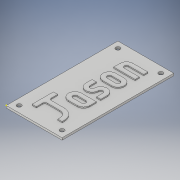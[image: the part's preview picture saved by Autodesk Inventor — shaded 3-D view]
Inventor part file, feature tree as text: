
AUTODESK INVENTOR PART (.ipt)
format: ipt  version: 2017 (Build 210142000, 142)  size: 196,096 bytes
history: native  units: in
note: dims shown in document units (in); Inventor stores cm internally (conversion verified against a paired STEP export)
features: sketch x4, extrude x3, projected_geometry x1
ambient origin geometry x8: Origin, YZ Plane, XZ Plane, XY Plane, X Axis, Y Axis, Z Axis, Center Point
bodies: Solid1 (feature_tree)
feature tree (8):
  extrude  "Extrusion1"  Depth=0.0625in TaperAngle=0.0deg
  sketch  "Sketch2"  dims[d6=0.0625in d7=0.0in]
  sketch  "Sketch3"
  extrude  "Extrusion2"  [1 undecoded]
  extrude  "Extrusion3"  [1 undecoded]
  sketch  "Sketch1"  dims[d2=0.125in d3=0.0in d4=0.0625in d5=0.0in]
  sketch  "Sketch4"
  projected_geometry  "Projected Loop1"
note: 2 required parameter values undecoded (feature->parameter linkage not recoverable at this tier; creation-order binding heuristic only, values carry confidence <= 0.55)
